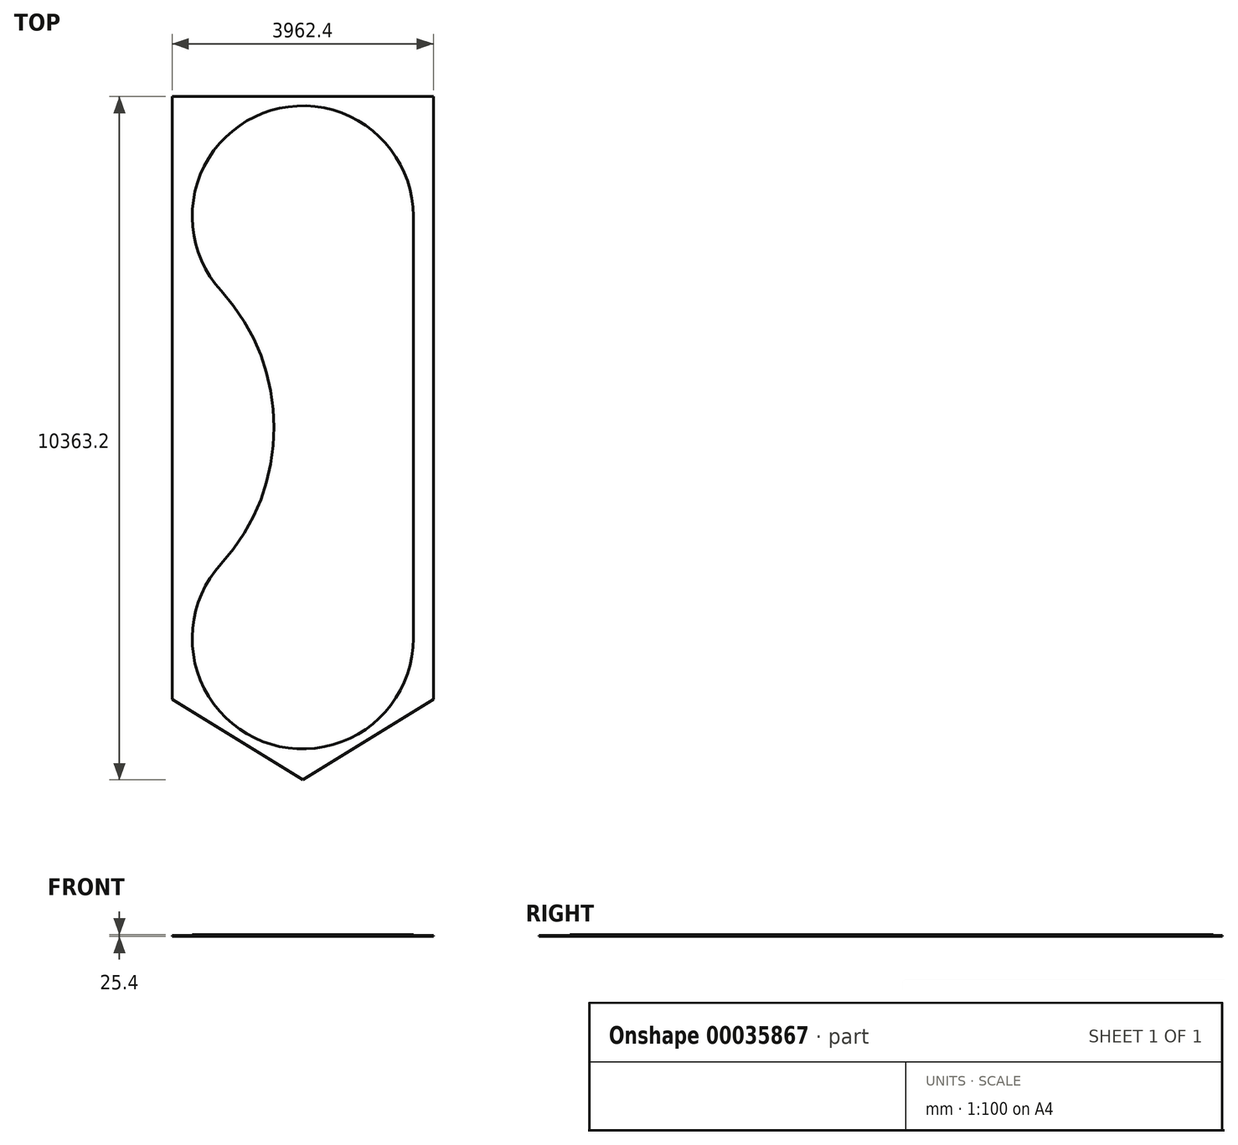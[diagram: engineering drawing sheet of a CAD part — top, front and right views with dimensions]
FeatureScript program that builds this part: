
annotation { "Feature Type Name" : "Feature", "Feature Type Description" : "" }
export const myFeature = defineFeature(function(context is Context, id is Id, definition is map)
    precondition{}
    {
        {
            var Q0;
            Q0=qCreatedBy(makeId("Top.planeOp"),FACE);
            var sketch = newSketch(context, id + "F0", { "sketchPlane" : qUnion([Q0])});
            skLineSegment(sketch, "E0", {"start": v(0, -3200.4) * mm, "end": v(0, 3200.4) * mm});
            skArc(sketch, "E1", {"start": v(-2914.4, -2070.06) * mm, "mid": v(-2111.53, 0) * mm, "end": v(-2914.4, 2070.06) * mm});
            skArc(sketch, "E2", {"start": v(0, 3200.4) * mm, "mid": v(-2282.6, 4763.36) * mm, "end": v(-2914.4, 2070.06) * mm});
            skArc(sketch, "E3", {"start": v(-2914.4, -2070.06) * mm, "mid": v(-2282.6, -4763.36) * mm, "end": v(0, -3200.4) * mm});
            skPoint(sketch, "E4", {"position": v(0, 1981.2) * mm});
            skPoint(sketch, "E5", {"position": v(0, 762) * mm});
            skPoint(sketch, "E6", {"position": v(-435.7, 4327.77) * mm});
            skPoint(sketch, "E7", {"position": v(-3352.47, 3167.27) * mm});
            skPoint(sketch, "E8", {"position": v(-1566.9, 4873.22) * mm});
            skPoint(sketch, "E9", {"position": v(-2917.1, 4327.77) * mm});
            skPoint(sketch, "E10", {"position": v(0, -762) * mm});
            skPoint(sketch, "E11", {"position": v(0, -1981.2) * mm});
            skPoint(sketch, "E12", {"position": v(-437.93, -4330.23) * mm});
            skPoint(sketch, "E13", {"position": v(-1590.82, -4874.61) * mm});
            skPoint(sketch, "E14", {"position": v(-2914.87, -4330.23) * mm});
            skPoint(sketch, "E15", {"position": v(-3352.05, -3150.18) * mm});
            skPoint(sketch, "E16", {"position": v(-2111.53, 0) * mm});
            skPoint(sketch, "E17", {"position": v(-2302.84, 1066.8) * mm});
            skPoint(sketch, "E18", {"position": v(-2302.84, -1066.8) * mm});
            skSolve(sketch);
        }
        {
            var Q0;
            Q0=qCreatedBy(makeId("Top.planeOp"),FACE);
            var sketch = newSketch(context, id + "F1", { "sketchPlane" : qUnion([Q0])});
            skLineSegment(sketch, "E19.bottom", {"start": v(-3657.6, 5017.18) * mm, "end": v(304.8, 5017.18) * mm});
            skLineSegment(sketch, "E19.left", {"start": v(-3657.6, 5017.18) * mm, "end": v(-3657.6, -4126.82) * mm});
            skLineSegment(sketch, "E19.right", {"start": v(304.8, 5017.18) * mm, "end": v(304.8, -4126.82) * mm});
            skLineSegment(sketch, "E20", {"start": v(-3657.6, -4126.82) * mm, "end": v(-1676.4, -5346.02) * mm});
            skLineSegment(sketch, "E21", {"start": v(-1676.4, -5346.02) * mm, "end": v(304.8, -4126.82) * mm});
            skSolve(sketch);
        }
        {
            var Q0;
            Q0=makeQuery(id+"F0.imprint","IMPRINT",FACE,{"disambiguationData":[TD([[makeQuery(id+"F0.imprint","IMPRINT",EDGE,{"derivedFrom":sQuery(id+"F0.wireOp",EDGE,"E0")}),1.0]])]});
            extrude(context, id + "F2", {"entities" : qUnion([Q0]), "depth" : 25.4 * mm});
        }
        {
            var Q0;
            Q0=makeQuery(id+"F1.imprint","IMPRINT",FACE,{"disambiguationData":[TD([[makeQuery(id+"F1.imprint","IMPRINT",EDGE,{"derivedFrom":sQuery(id+"F1.wireOp",EDGE,"E19.bottom")}),-1.0]])]});
            extrude(context, id + "F3", {"entities" : qUnion([Q0]), "operationType" : NewBodyOperationType.ADD, "depth" : 12.7 * mm});
        }
    });
